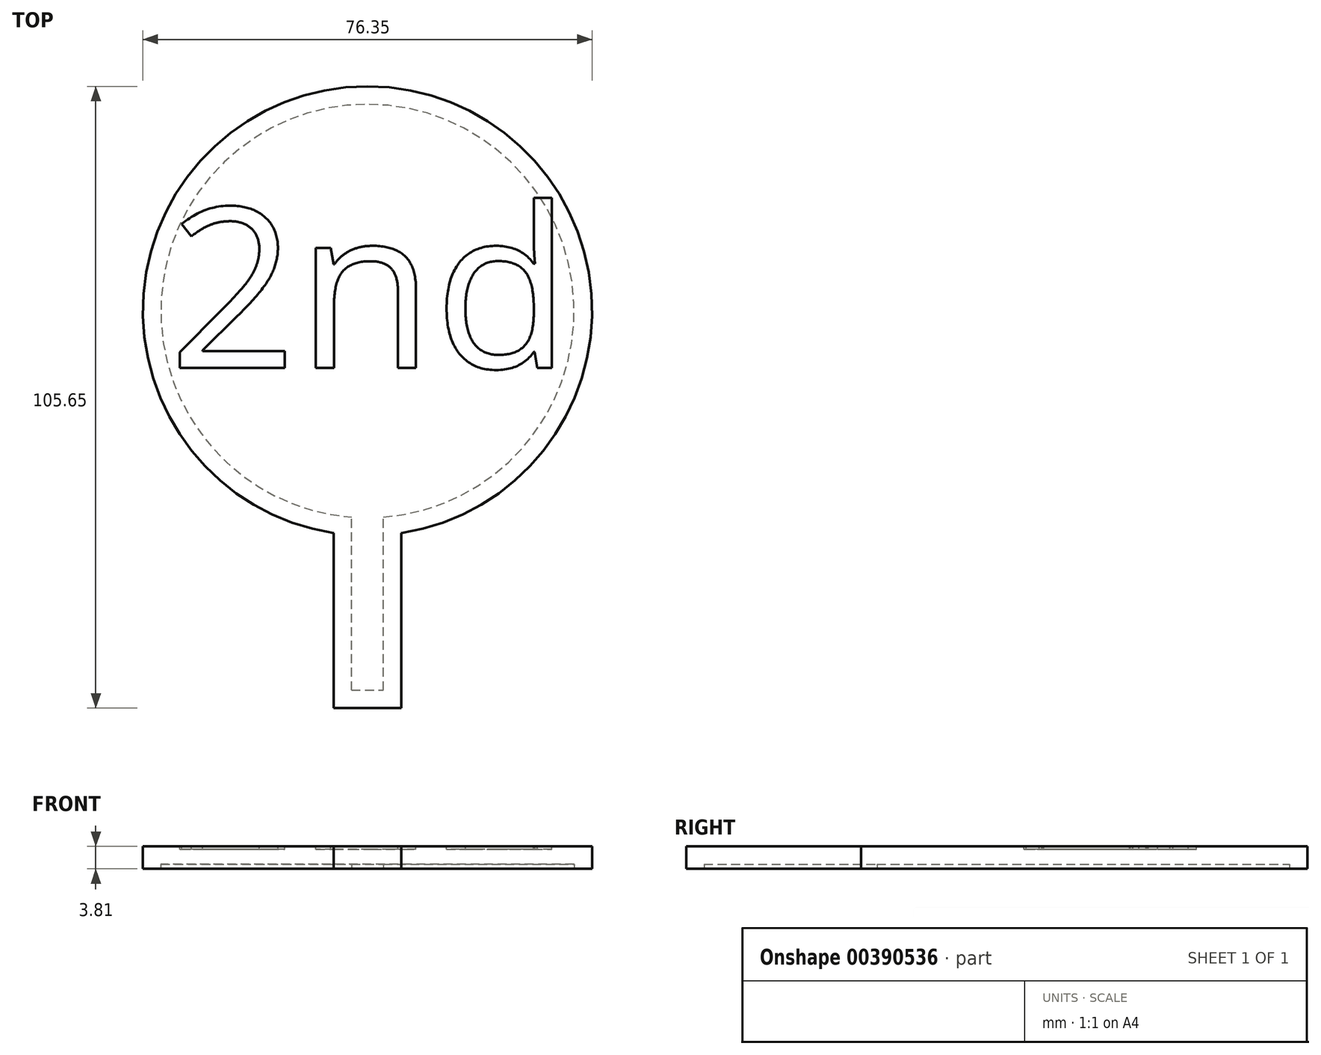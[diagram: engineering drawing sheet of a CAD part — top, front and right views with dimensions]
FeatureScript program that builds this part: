
annotation { "Feature Type Name" : "Feature", "Feature Type Description" : "" }
export const myFeature = defineFeature(function(context is Context, id is Id, definition is map)
    precondition{}
    {
        {
            var Q0;
            Q0=qCreatedBy(makeId("Top.planeOp"),FACE);
            var sketch = newSketch(context, id + "F0", { "sketchPlane" : qUnion([Q0])});
            skLineSegment(sketch, "E0", {"start": v(-13.52, -35.14) * mm, "end": v(-1.98, -35.14) * mm});
            skLineSegment(sketch, "E1", {"start": v(-1.98, -35.14) * mm, "end": v(-1.98, -5.4) * mm});
            skLineSegment(sketch, "E2", {"start": v(-13.52, -35.14) * mm, "end": v(-13.52, -5.4) * mm});
            skArc(sketch, "E3", {"start": v(-1.98, -5.4) * mm, "mid": v(-7.75, 70.5) * mm, "end": v(-13.52, -5.4) * mm});
            skSolve(sketch);
        }
        {
            var Q0;
            Q0=makeQuery(id+"F0.imprint","IMPRINT",FACE,{"disambiguationData":[TD([[makeQuery(id+"F0.imprint","IMPRINT",EDGE,{"derivedFrom":sQuery(id+"F0.wireOp",EDGE,"E0")}),1.0]])]});
            extrude(context, id + "F1", {"entities" : qUnion([Q0]), "depth" : 3.8 * mm});
        }
        {
            var Q0;
            Q0=makeQuery(id+"F1.opExtrude","CAP_FACE",FACE,{"disambiguationData":[OSD([sQuery(id+"F0.wireOp",EDGE,"E0"),sQuery(id+"F0.wireOp",EDGE,"E1"),sQuery(id+"F0.wireOp",EDGE,"E2"),sQuery(id+"F0.wireOp",EDGE,"E3")])],"isStart":true});
            shell(context, id + "F2", {"entities" : qUnion([Q0]), "thickness" : 3.05 * mm});
        }
        {
            var Q0;
            Q0=makeQuery(id+"F1.opExtrude","CAP_FACE",FACE,{"disambiguationData":[OSD([sQuery(id+"F0.wireOp",EDGE,"E0"),sQuery(id+"F0.wireOp",EDGE,"E1"),sQuery(id+"F0.wireOp",EDGE,"E2"),sQuery(id+"F0.wireOp",EDGE,"E3")])],"isStart":false});
            var sketch = newSketch(context, id + "F3", { "sketchPlane" : qUnion([Q0])});
            skText(sketch, "E4", { "text": "2nd", "fontName": "OpenSans-Regular.ttf"});
            const initialGuessF3  = {"E4": [-0.04155, 0.02267, 1, 0, 0.0274]};
            skSetInitialGuess(sketch, initialGuessF3);
            skSolve(sketch);
        }
        {
            var Q0;
            Q0=qSketchRegion(id+"F3",true);
            extrude(context, id + "F4", {"entities" : qUnion([Q0]), "operationType" : NewBodyOperationType.REMOVE, "oppositeDirection" : true, "depth" : 0.5 * mm});
        }
    });
